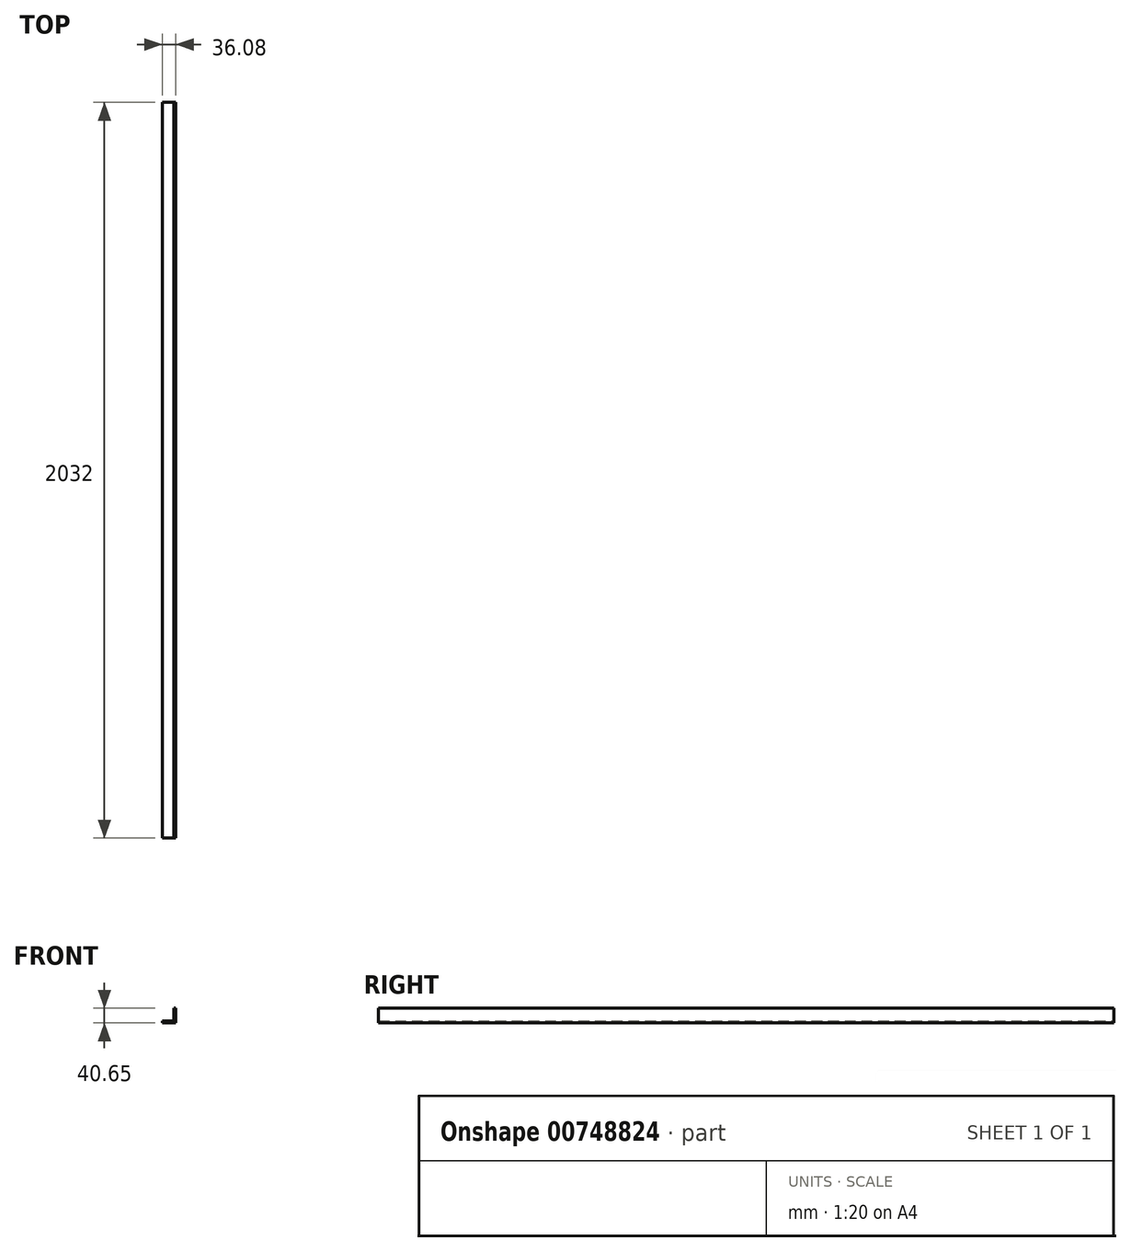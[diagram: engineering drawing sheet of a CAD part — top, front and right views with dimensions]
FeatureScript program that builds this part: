
annotation { "Feature Type Name" : "Feature", "Feature Type Description" : "" }
export const myFeature = defineFeature(function(context is Context, id is Id, definition is map)
    precondition{}
    {
        {
            var Q0;
            Q0=qCreatedBy(makeId("Front.planeOp"),FACE);
            var sketch = newSketch(context, id + "F0", { "sketchPlane" : qUnion([Q0])});
            skLineSegment(sketch, "E0.bottom", {"start": v(-113.5, 76.96) * mm, "end": v(-118.07, 76.96) * mm});
            skLineSegment(sketch, "E0.top", {"start": v(-113.5, 36.31) * mm, "end": v(-118.07, 36.31) * mm});
            skLineSegment(sketch, "E0.left", {"start": v(-113.5, 76.96) * mm, "end": v(-113.5, 36.31) * mm});
            skLineSegment(sketch, "E0.right", {"start": v(-118.07, 76.96) * mm, "end": v(-118.07, 36.31) * mm});
            skLineSegment(sketch, "E1.bottom", {"start": v(-118.07, 42.25) * mm, "end": v(-149.58, 42.25) * mm});
            skLineSegment(sketch, "E1.top", {"start": v(-118.07, 36.31) * mm, "end": v(-149.58, 36.31) * mm});
            skLineSegment(sketch, "E1.left", {"start": v(-118.07, 42.25) * mm, "end": v(-118.07, 36.31) * mm});
            skLineSegment(sketch, "E1.right", {"start": v(-149.58, 42.25) * mm, "end": v(-149.58, 36.31) * mm});
            skSolve(sketch);
        }
        {
            var Q0;
            Q0=makeQuery(id+"F0.imprint","IMPRINT",FACE,{"disambiguationData":[TD([[makeQuery(id+"F0.imprint","IMPRINT",EDGE,{"derivedFrom":sQuery(id+"F0.wireOp",EDGE,"E0.bottom")}),1.0]])]});
            var Q1;
            Q1=makeQuery(id+"F0.imprint","IMPRINT",FACE,{"disambiguationData":[TD([[makeQuery(id+"F0.imprint","IMPRINT",EDGE,{"derivedFrom":sQuery(id+"F0.wireOp",EDGE,"E1.bottom")}),1.0]])]});
            extrude(context, id + "F1", {"entities" : qUnion([Q0, Q1]), "depth" : 2032 * mm, "offsetDistance" : 25.4 * mm});
        }
    });
